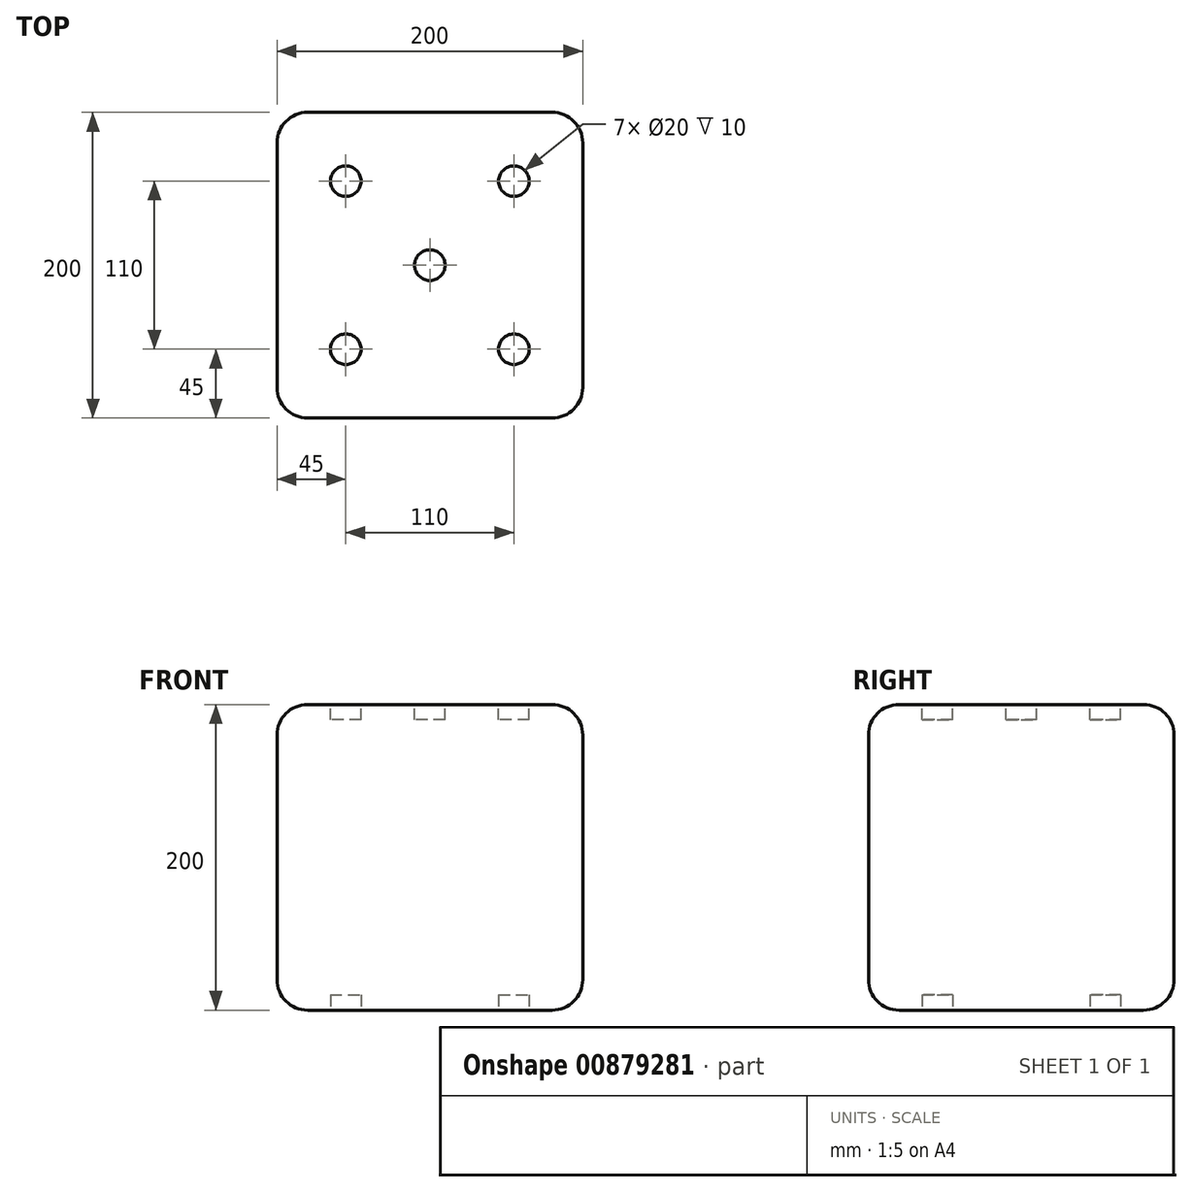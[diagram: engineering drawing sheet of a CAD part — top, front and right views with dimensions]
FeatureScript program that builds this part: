
annotation { "Feature Type Name" : "Feature", "Feature Type Description" : "" }
export const myFeature = defineFeature(function(context is Context, id is Id, definition is map)
    precondition{}
    {
        {
            assignVariable(context, id + "F0", {"name" : "Length", "anyValue" : 200});
        }
        {
            var Q0;
            Q0=qCreatedBy(makeId("Top.planeOp"),FACE);
            var sketch = newSketch(context, id + "F1", { "sketchPlane" : qUnion([Q0])});
            skLineSegment(sketch, "E0.bottom", {"start": v(-100, -100) * mm, "end": v(100, -100) * mm});
            skLineSegment(sketch, "E0.top", {"start": v(-100, 100) * mm, "end": v(100, 100) * mm});
            skLineSegment(sketch, "E0.left", {"start": v(-100, -100) * mm, "end": v(-100, 100) * mm});
            skLineSegment(sketch, "E0.right", {"start": v(100, -100) * mm, "end": v(100, 100) * mm});
            skSolve(sketch);
        }
        {
            var Q0;
            Q0 = qSketchRegion(id + "F1", true);
            extrude(context, id + "F2", {"entities" : qUnion([Q0]), "endBound" : BoundingType.SYMMETRIC, "depth" : (getVariable(context, 'Length')) * mm, "offsetDistance" : 25 * mm});
        }
        {
            var Q0;
            Q0=makeQuery(id+"F2.opExtrude","CAP_FACE",FACE,{"disambiguationData":[OSD([sQuery(id+"F1.wireOp",EDGE,"E0.bottom"),sQuery(id+"F1.wireOp",EDGE,"E0.top"),sQuery(id+"F1.wireOp",EDGE,"E0.left"),sQuery(id+"F1.wireOp",EDGE,"E0.right")])],"isStart":false});
            var Q1;
            Q1=makeQuery(id+"F2.opExtrude","SWEPT_FACE",FACE,{"disambiguationData":[OSD([sQuery(id+"F1.wireOp",EDGE,"E0.bottom")])]});
            var Q2;
            Q2=makeQuery(id+"F2.opExtrude","SWEPT_FACE",FACE,{"disambiguationData":[OSD([sQuery(id+"F1.wireOp",EDGE,"E0.right")])]});
            var Q3;
            Q3=makeQuery(id+"F2.opExtrude","CAP_FACE",FACE,{"disambiguationData":[OSD([sQuery(id+"F1.wireOp",EDGE,"E0.bottom"),sQuery(id+"F1.wireOp",EDGE,"E0.top"),sQuery(id+"F1.wireOp",EDGE,"E0.left"),sQuery(id+"F1.wireOp",EDGE,"E0.right")])],"isStart":true});
            var Q4;
            Q4=makeQuery(id+"F2.opExtrude","SWEPT_FACE",FACE,{"disambiguationData":[OSD([sQuery(id+"F1.wireOp",EDGE,"E0.top")])]});
            var Q5;
            Q5=makeQuery(id+"F2.opExtrude","SWEPT_FACE",FACE,{"disambiguationData":[OSD([sQuery(id+"F1.wireOp",EDGE,"E0.left")])]});
            fillet(context, id + "F3", {"entities" : qUnion([Q0, Q1, Q2, Q3, Q4, Q5]), "radius" : (getVariable(context, 'Length') / 10) * mm, "tangentPropagation" : true, "allowEdgeOverflow" : false});
        }
        {
            var Q0;
            Q0=makeQuery(id+"F2.opExtrude","CAP_FACE",FACE,{"disambiguationData":[OSD([sQuery(id+"F1.wireOp",EDGE,"E0.bottom"),sQuery(id+"F1.wireOp",EDGE,"E0.top"),sQuery(id+"F1.wireOp",EDGE,"E0.left"),sQuery(id+"F1.wireOp",EDGE,"E0.right")])],"isStart":false});
            var sketch = newSketch(context, id + "F4", { "sketchPlane" : qUnion([Q0])});
            skLineSegment(sketch, "E1", {"start": v(-80, 80) * mm, "end": v(80, -80) * mm, "construction": true});
            skLineSegment(sketch, "E2", {"start": v(80, 80) * mm, "end": v(-80, -80) * mm, "construction": true});
            skCircle(sketch, "E3", {"center": v(0, 0) * mm, "radius": 10 * mm});
            skLineSegment(sketch, "E4", {"start": v(-55, 55) * mm, "end": v(55, 55) * mm, "construction": true});
            skLineSegment(sketch, "E5", {"start": v(-55, -55) * mm, "end": v(55, -55) * mm, "construction": true});
            skCircle(sketch, "E6", {"center": v(-55, 55) * mm, "radius": 10 * mm});
            skCircle(sketch, "E7", {"center": v(55, 55) * mm, "radius": 10 * mm});
            skCircle(sketch, "E8", {"center": v(55, -55) * mm, "radius": 10 * mm});
            skCircle(sketch, "E9", {"center": v(-55, -55) * mm, "radius": 10 * mm});
            skSolve(sketch);
        }
        {
            var Q0;
            Q0 = qSketchRegion(id + "F4", true);
            extrude(context, id + "F5", {"entities" : qUnion([Q0]), "operationType" : NewBodyOperationType.REMOVE, "oppositeDirection" : true, "depth" : (getVariable(context, 'Length') / 20) * mm, "offsetDistance" : 25 * mm});
        }
        {
            var Q0;
            Q0=makeQuery(id+"F2.opExtrude","CAP_FACE",FACE,{"disambiguationData":[OSD([sQuery(id+"F1.wireOp",EDGE,"E0.bottom"),sQuery(id+"F1.wireOp",EDGE,"E0.top"),sQuery(id+"F1.wireOp",EDGE,"E0.left"),sQuery(id+"F1.wireOp",EDGE,"E0.right")])],"isStart":true});
            var sketch = newSketch(context, id + "F6", { "sketchPlane" : qUnion([Q0])});
            skLineSegment(sketch, "E10", {"start": v(-80, -80) * mm, "end": v(80, 80) * mm, "construction": true});
            skLineSegment(sketch, "E11", {"start": v(-80, 80) * mm, "end": v(80, -80) * mm, "construction": true});
            skLineSegment(sketch, "E12", {"start": v(-55, 55) * mm, "end": v(55, 55) * mm, "construction": true});
            skLineSegment(sketch, "E13", {"start": v(-55, -55) * mm, "end": v(55, -55) * mm, "construction": true});
            skCircle(sketch, "E14", {"center": v(55, 55) * mm, "radius": 10 * mm});
            skCircle(sketch, "E15", {"center": v(-55, -55) * mm, "radius": 10 * mm});
            skSolve(sketch);
        }
        {
            var Q0;
            Q0 = qSketchRegion(id + "F6", true);
            extrude(context, id + "F7", {"entities" : qUnion([Q0]), "operationType" : NewBodyOperationType.REMOVE, "oppositeDirection" : true, "depth" : (getVariable(context, 'Length') / 20) * mm, "offsetDistance" : 25 * mm});
        }
    });
